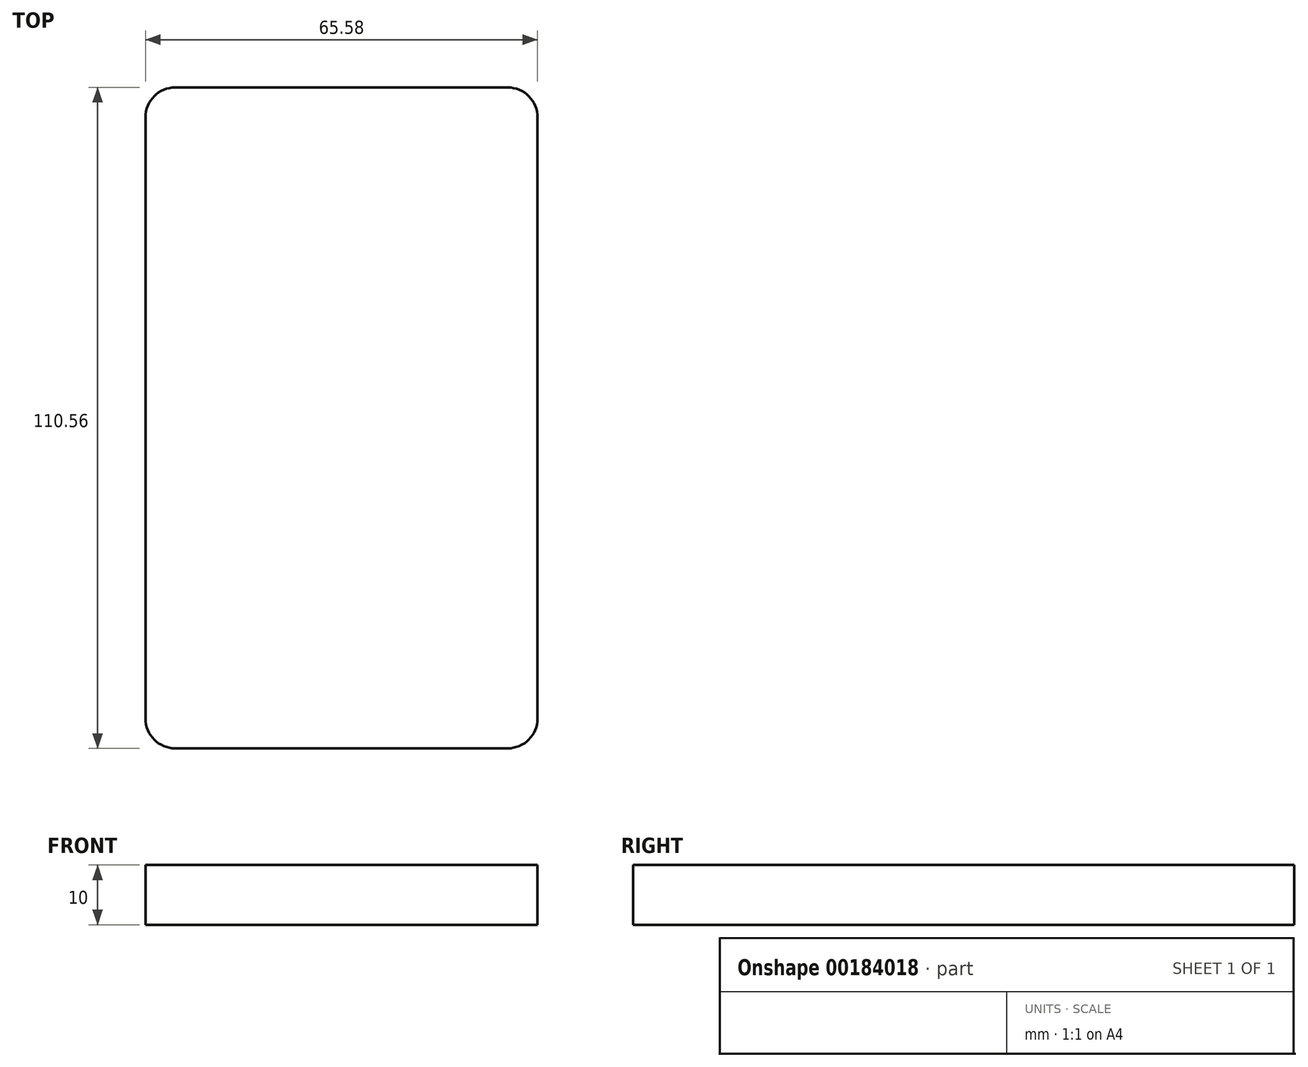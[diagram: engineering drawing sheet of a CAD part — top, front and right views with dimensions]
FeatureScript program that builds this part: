
annotation { "Feature Type Name" : "Feature", "Feature Type Description" : "" }
export const myFeature = defineFeature(function(context is Context, id is Id, definition is map)
    precondition{}
    {
        {
            var Q0;
            Q0=qCreatedBy(makeId("Top.planeOp"),FACE);
            var sketch = newSketch(context, id + "F0", { "sketchPlane" : qUnion([Q0])});
            skLineSegment(sketch, "E0.bottom", {"start": v(32.8, 55.28) * mm, "end": v(-32.8, 55.28) * mm});
            skLineSegment(sketch, "E0.top", {"start": v(32.8, -55.28) * mm, "end": v(-32.8, -55.28) * mm});
            skLineSegment(sketch, "E0.left", {"start": v(32.8, 55.28) * mm, "end": v(32.8, -55.28) * mm});
            skLineSegment(sketch, "E0.right", {"start": v(-32.8, 55.28) * mm, "end": v(-32.8, -55.28) * mm});
            skPoint(sketch, "E0.middle", {"position": v(0, 0) * mm});
            skSolve(sketch);
        }
        {
            var Q0;
            Q0=makeQuery(id+"F0.imprint","IMPRINT",FACE,{"disambiguationData":[TD([[makeQuery(id+"F0.imprint","IMPRINT",EDGE,{"derivedFrom":sQuery(id+"F0.wireOp",EDGE,"E0.bottom")}),1.0]])]});
            extrude(context, id + "F1", {"entities" : qUnion([Q0]), "depth" : 10 * mm});
        }
        {
            var Q0;
            Q0=makeQuery(id+"F1.opExtrude","SWEPT_EDGE",EDGE,{"disambiguationData":[OSD([sQuery(id+"F0.wireOp",EDGE,"E0.bottom"),sQuery(id+"F0.wireOp",EDGE,"E0.left")])]});
            var Q1;
            Q1=makeQuery(id+"F1.opExtrude","SWEPT_EDGE",EDGE,{"disambiguationData":[OSD([sQuery(id+"F0.wireOp",EDGE,"E0.bottom"),sQuery(id+"F0.wireOp",EDGE,"E0.right")])]});
            fillet(context, id + "F2", {"entities" : qUnion([Q0, Q1]), "radius" : 5 * mm, "tangentPropagation" : true, "allowEdgeOverflow" : false});
        }
        {
            var Q0;
            Q0=makeQuery(id+"F1.opExtrude","SWEPT_EDGE",EDGE,{"disambiguationData":[OSD([sQuery(id+"F0.wireOp",EDGE,"E0.top"),sQuery(id+"F0.wireOp",EDGE,"E0.left")])]});
            var Q1;
            Q1=makeQuery(id+"F1.opExtrude","SWEPT_EDGE",EDGE,{"disambiguationData":[OSD([sQuery(id+"F0.wireOp",EDGE,"E0.top"),sQuery(id+"F0.wireOp",EDGE,"E0.right")])]});
            fillet(context, id + "F3", {"entities" : qUnion([Q0, Q1]), "radius" : 5 * mm, "tangentPropagation" : true, "allowEdgeOverflow" : false});
        }
    });
